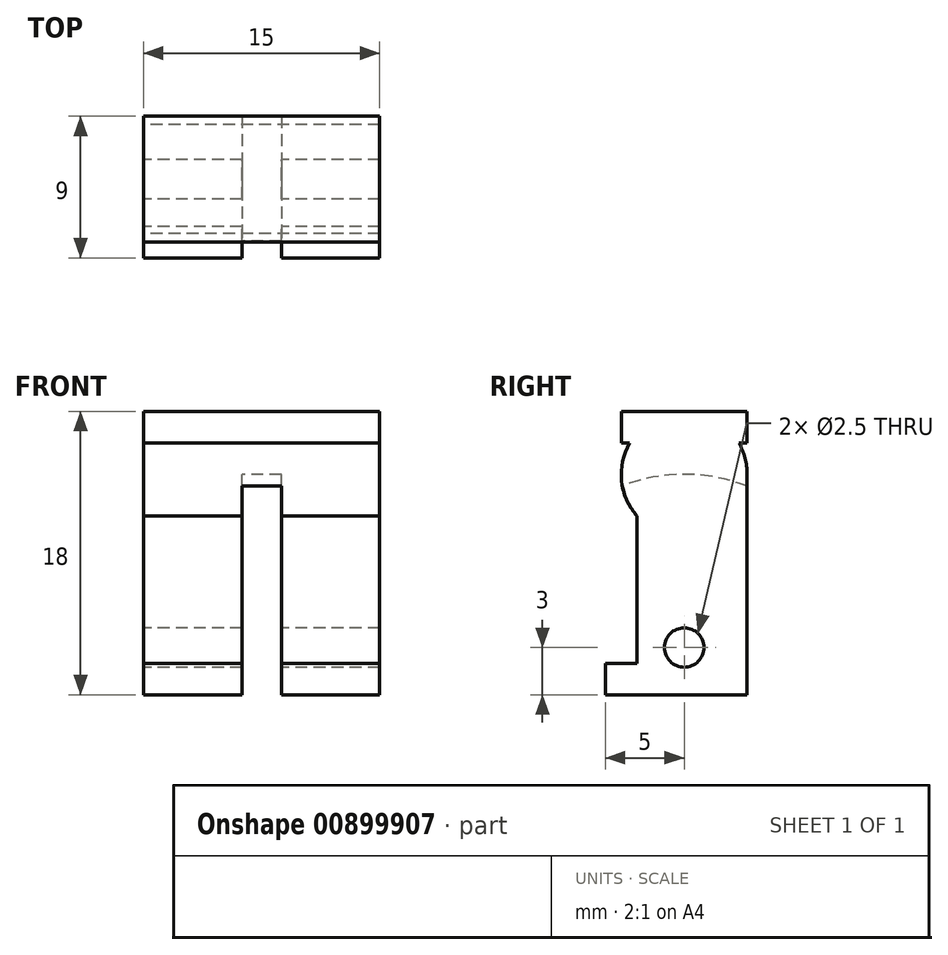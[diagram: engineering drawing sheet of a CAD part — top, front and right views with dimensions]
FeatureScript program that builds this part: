
annotation { "Feature Type Name" : "Feature", "Feature Type Description" : "" }
export const myFeature = defineFeature(function(context is Context, id is Id, definition is map)
    precondition{}
    {
        {
            var Q0;
            Q0=qCreatedBy(makeId("Right.planeOp"),FACE);
            var sketch = newSketch(context, id + "F0", { "sketchPlane" : qUnion([Q0])});
            skLineSegment(sketch, "E0.bottom", {"start": v(4, 1) * mm, "end": v(-4, 1) * mm});
            skLineSegment(sketch, "E0.top", {"start": v(4, -1) * mm, "end": v(3.46, -1) * mm});
            skLineSegment(sketch, "E0.left", {"start": v(4, 1) * mm, "end": v(4, -1) * mm});
            skLineSegment(sketch, "E0.right", {"start": v(-4, 1) * mm, "end": v(-4, -1) * mm});
            skPoint(sketch, "E0.middle", {"position": v(0, 0) * mm});
            skArc(sketch, "E1", {"start": v(-3.46, -1) * mm, "mid": v(-3.98, -3.4) * mm, "end": v(-3, -5.65) * mm});
            skLineSegment(sketch, "E2.top", {"start": v(0.75, -15) * mm, "end": v(-0.75, -15) * mm});
            skLineSegment(sketch, "E2.left", {"start": v(4, -3) * mm, "end": v(4, -15) * mm});
            skLineSegment(sketch, "E2.right", {"start": v(-3, -5.65) * mm, "end": v(-3, -15) * mm});
            skLineSegment(sketch, "E3.top", {"start": v(4, -17) * mm, "end": v(-5, -17) * mm});
            skLineSegment(sketch, "E3.left", {"start": v(4, -15) * mm, "end": v(4, -17) * mm});
            skLineSegment(sketch, "E3.right", {"start": v(-5, -15) * mm, "end": v(-5, -17) * mm});
            skCircle(sketch, "E4", {"center": v(0, -14) * mm, "radius": 1.25 * mm});
            skLineSegment(sketch, "E5.trimOffspring", {"start": v(-3.46, -1) * mm, "end": v(-4, -1) * mm});
            skArc(sketch, "E6.trimOffspring", {"start": v(4, -3) * mm, "mid": v(3.86, -1.96) * mm, "end": v(3.46, -1) * mm});
            skLineSegment(sketch, "E7.trimOffspring", {"start": v(-3, -15) * mm, "end": v(-5, -15) * mm});
            skSolve(sketch);
        }
        {
            var Q0;
            Q0 = qSketchRegion(id + "F0", true);
            extrude(context, id + "F1", {"entities" : qUnion([Q0]), "endBound" : BoundingType.SYMMETRIC, "depth" : 15 * mm, "offsetDistance" : 25.4 * mm});
        }
        {
            var Q0;
            Q0=qCreatedBy(makeId("Right.planeOp"),FACE);
            var sketch = newSketch(context, id + "F2", { "sketchPlane" : qUnion([Q0])});
            skCircle(sketch, "E8", {"center": v(0, -14) * mm, "radius": 11 * mm});
            skSolve(sketch);
        }
        {
            var Q0;
            Q0=makeQuery(id+"F2.imprint","IMPRINT",FACE,{"disambiguationData":[TD([[makeQuery(id+"F2.imprint","IMPRINT",EDGE,{"derivedFrom":sQuery(id+"F2.wireOp",EDGE,"E8")}),1.0]])]});
            extrude(context, id + "F3", {"entities" : qUnion([Q0]), "operationType" : NewBodyOperationType.REMOVE, "endBound" : BoundingType.SYMMETRIC, "depth" : 2.5 * mm, "offsetDistance" : 25.4 * mm});
        }
    });
